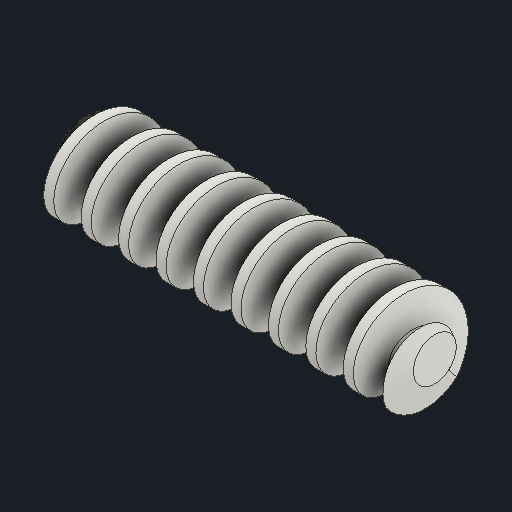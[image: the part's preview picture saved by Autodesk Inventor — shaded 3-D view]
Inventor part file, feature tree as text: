
AUTODESK INVENTOR PART (.ipt)
format: ipt  version: 2024 (Build 280153000, 153)  size: 339,968 bytes
history: native  units: mm (DEFAULTED — no unit token found)
features: other x5, chamfer x2, pattern_circular x2, extrude x1
ambient origin geometry x6: Origin, XZ Plane, X Axis, Y Axis, Z Axis, Center Point
bodies: Solid1 (feature_tree)
feature tree (10):
  extrude  "기본 본체"  Depth=40.0mm
  chamfer  "Chamfer1"  Distance=16.0mm
  chamfer  "Chamfer2"  Distance=60.0mm
  other  "톱니 스케치"
  pattern_circular  "톱니 패턴"  [2 undecoded]
  other  "왼쪽 톱니"
  pattern_circular  "왼쪽 톱니 패턴"  [2 undecoded]
  other  "기본 본체 스케치"
  other  "Srf1"
  other  "피치 지름"
note: 4 required parameter values undecoded (feature->parameter linkage not recoverable at this tier; creation-order binding heuristic only, values carry confidence <= 0.55)
